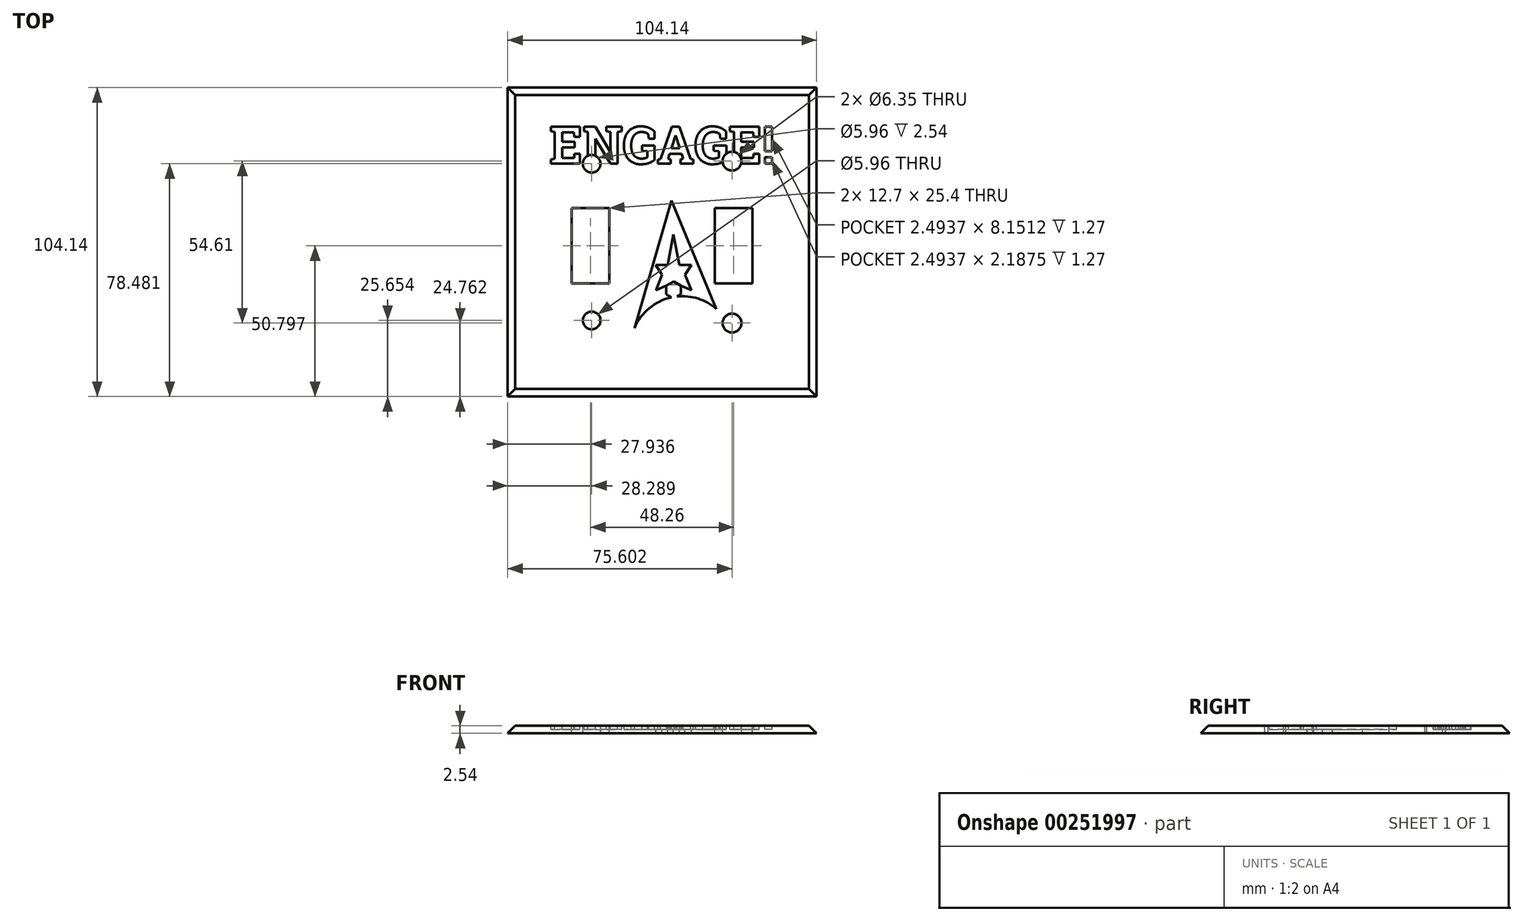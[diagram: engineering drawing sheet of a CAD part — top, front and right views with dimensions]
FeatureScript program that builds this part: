
annotation { "Feature Type Name" : "Feature", "Feature Type Description" : "" }
export const myFeature = defineFeature(function(context is Context, id is Id, definition is map)
    precondition{}
    {
        {
            var Q0;
            Q0=qCreatedBy(makeId("Top.planeOp"),FACE);
            var sketch = newSketch(context, id + "F0", { "sketchPlane" : qUnion([Q0])});
            skLineSegment(sketch, "E0.bottom", {"start": v(-65.17, 86.13) * mm, "end": v(49.13, 86.13) * mm});
            skLineSegment(sketch, "E0.top", {"start": v(-65.17, -28.17) * mm, "end": v(49.13, -28.17) * mm});
            skLineSegment(sketch, "E0.left", {"start": v(-65.17, 86.13) * mm, "end": v(-65.17, -28.17) * mm});
            skLineSegment(sketch, "E0.right", {"start": v(49.13, 86.13) * mm, "end": v(49.13, -28.17) * mm});
            skSolve(sketch);
        }
        {
            var Q0;
            Q0=makeQuery(id+"F0.imprint","IMPRINT",FACE,{"disambiguationData":[TD([[makeQuery(id+"F0.imprint","IMPRINT",EDGE,{"derivedFrom":sQuery(id+"F0.wireOp",EDGE,"E0.bottom")}),-1.0]])]});
            extrude(context, id + "F1", {"entities" : qUnion([Q0]), "depth" : 2.54 * mm});
        }
        {
            var Q0;
            Q0=makeQuery(id+"F1.opExtrude","CAP_EDGE",EDGE,{"disambiguationData":[OSD([sQuery(id+"F0.wireOp",EDGE,"E0.top")])],"isStart":false});
            var Q1;
            Q1=makeQuery(id+"F1.opExtrude","CAP_EDGE",EDGE,{"disambiguationData":[OSD([sQuery(id+"F0.wireOp",EDGE,"E0.left")])],"isStart":false});
            var Q2;
            Q2=makeQuery(id+"F1.opExtrude","CAP_EDGE",EDGE,{"disambiguationData":[OSD([sQuery(id+"F0.wireOp",EDGE,"E0.right")])],"isStart":false});
            var Q3;
            Q3=makeQuery(id+"F1.opExtrude","CAP_EDGE",EDGE,{"disambiguationData":[OSD([sQuery(id+"F0.wireOp",EDGE,"E0.bottom")])],"isStart":false});
            chamfer(context, id + "F2", {"entities" : qUnion([Q0, Q1, Q2, Q3]), "width" : 7.62 * mm, "tangentPropagation" : true});
        }
        {
            var Q0;
            Q0=makeQuery(id+"F1.opExtrude","CAP_FACE",FACE,{"disambiguationData":[OSD([sQuery(id+"F0.wireOp",EDGE,"E0.bottom"),sQuery(id+"F0.wireOp",EDGE,"E0.top"),sQuery(id+"F0.wireOp",EDGE,"E0.left"),sQuery(id+"F0.wireOp",EDGE,"E0.right")])],"isStart":false});
            var sketch = newSketch(context, id + "F3", { "sketchPlane" : qUnion([Q0])});
            skLineSegment(sketch, "E1.bottom", {"start": v(-25.8, 15) * mm, "end": v(-38.5, 15) * mm});
            skLineSegment(sketch, "E1.top", {"start": v(-25.8, 40.4) * mm, "end": v(-38.5, 40.4) * mm});
            skLineSegment(sketch, "E1.left", {"start": v(-25.8, 15) * mm, "end": v(-25.8, 40.4) * mm});
            skLineSegment(sketch, "E1.right", {"start": v(-38.5, 15) * mm, "end": v(-38.5, 40.4) * mm});
            skLineSegment(sketch, "E2.bottom", {"start": v(9.76, 40.4) * mm, "end": v(22.46, 40.4) * mm});
            skLineSegment(sketch, "E2.top", {"start": v(9.76, 15) * mm, "end": v(22.46, 15) * mm});
            skLineSegment(sketch, "E2.left", {"start": v(9.76, 40.4) * mm, "end": v(9.76, 15) * mm});
            skLineSegment(sketch, "E2.right", {"start": v(22.46, 40.4) * mm, "end": v(22.46, 15) * mm});
            skSolve(sketch);
        }
        {
            var Q0;
            Q0 = qSketchRegion(id + "F3", true);
            extrude(context, id + "F4", {"entities" : qUnion([Q0]), "operationType" : NewBodyOperationType.REMOVE, "oppositeDirection" : true, "depth" : 25.4 * mm});
        }
        {
            var Q0;
            Q0=makeQuery(id+"F1.opExtrude","CAP_FACE",FACE,{"disambiguationData":[OSD([sQuery(id+"F0.wireOp",EDGE,"E0.bottom"),sQuery(id+"F0.wireOp",EDGE,"E0.top"),sQuery(id+"F0.wireOp",EDGE,"E0.left"),sQuery(id+"F0.wireOp",EDGE,"E0.right")])],"isStart":false});
            var sketch = newSketch(context, id + "F5", { "sketchPlane" : qUnion([Q0])});
            skText(sketch, "E3", { "text": "ENGAGE!", "fontName": "RobotoSlab-Bold.ttf"});
            const initialGuessF5  = {"E3": [-0.04604, 0.0554, 1, 0, 0.0126]};
            skSetInitialGuess(sketch, initialGuessF5);
            skSolve(sketch);
        }
        {
            var Q0;
            Q0 = qSketchRegion(id + "F5", true);
            extrude(context, id + "F6", {"entities" : qUnion([Q0]), "operationType" : NewBodyOperationType.REMOVE, "oppositeDirection" : true, "depth" : 1.27 * mm});
        }
        {
            var Q0;
            {var subQ0=sQuery(id+"F0.wireOp",EDGE,"E0.right");var subQ1=sQuery(id+"F0.wireOp",EDGE,"E0.left");var subQ2=sQuery(id+"F0.wireOp",EDGE,"E0.top");var subQ3=sQuery(id+"F0.wireOp",EDGE,"E0.bottom");Q0=makeQuery(id+"F6.boolean.opBoolean","SPLIT",FACE,{"disambiguationData":[TD([makeQuery(id+"F2.opChamfer","BLEND_FACE",FACE,{"disambiguationData":[OSD([subQ3])]})])],"derivedFrom":makeQuery(id+"F1.opExtrude","CAP_FACE",FACE,{"disambiguationData":[OSD([subQ3,subQ2,subQ1,subQ0])],"isStart":false})});}
            var sketch = newSketch(context, id + "F7", { "sketchPlane" : qUnion([Q0])});
            skArc(sketch, "E4", {"start": v(10.26, 6.47) * mm, "mid": v(-5.2, 10.28) * mm, "end": v(-17.36, 0) * mm});
            skLineSegment(sketch, "E5", {"start": v(-17.36, 0) * mm, "end": v(-4.93, 42.96) * mm});
            skLineSegment(sketch, "E6", {"start": v(-4.93, 42.96) * mm, "end": v(10.26, 6.47) * mm});
            skPoint(sketch, "E7.startSnap0", {"position": v(-11.15, 21.48) * mm});
            skCircle(sketch, "E8.cCircle", {"center": v(-4.21, 17.91) * mm, "radius": 3.35 * mm, "construction": true});
            skLineSegment(sketch, "E8.0", {"start": v(-2.27, 14.56) * mm, "end": v(-6.15, 14.56) * mm});
            skLineSegment(sketch, "E8.1", {"start": v(-6.15, 14.56) * mm, "end": v(-8.08, 17.91) * mm});
            skLineSegment(sketch, "E8.2", {"start": v(-8.08, 17.91) * mm, "end": v(-6.15, 21.27) * mm});
            skLineSegment(sketch, "E8.3", {"start": v(-6.15, 21.27) * mm, "end": v(-2.27, 21.27) * mm});
            skLineSegment(sketch, "E8.4", {"start": v(-2.27, 21.27) * mm, "end": v(-0.34, 17.91) * mm});
            skLineSegment(sketch, "E8.5", {"start": v(-0.34, 17.91) * mm, "end": v(-2.27, 14.56) * mm});
            skPoint(sketch, "E8.0.midPoint", {"position": v(-4.21, 14.56) * mm});
            skLineSegment(sketch, "E9", {"start": v(-8.08, 17.91) * mm, "end": v(-10.06, 12.78) * mm});
            skLineSegment(sketch, "E10", {"start": v(-10.06, 12.78) * mm, "end": v(-6.15, 14.56) * mm});
            skLineSegment(sketch, "E11", {"start": v(-2.27, 14.56) * mm, "end": v(1.8, 12.72) * mm});
            skLineSegment(sketch, "E12", {"start": v(1.8, 12.72) * mm, "end": v(-0.34, 17.91) * mm});
            skLineSegment(sketch, "E13", {"start": v(-8.08, 17.91) * mm, "end": v(-10.23, 21.22) * mm});
            skLineSegment(sketch, "E14", {"start": v(-10.23, 21.22) * mm, "end": v(-6.15, 21.27) * mm});
            skLineSegment(sketch, "E15", {"start": v(-2.27, 21.27) * mm, "end": v(1.8, 21.27) * mm});
            skLineSegment(sketch, "E16", {"start": v(1.8, 21.27) * mm, "end": v(-0.34, 17.91) * mm});
            skLineSegment(sketch, "E17", {"start": v(-6.15, 21.27) * mm, "end": v(-4.33, 31.55) * mm});
            skLineSegment(sketch, "E18", {"start": v(-4.33, 31.55) * mm, "end": v(-2.27, 21.27) * mm});
            skSolve(sketch);
        }
        {
            var Q0;
            Q0=makeQuery(id+"F7.imprint","IMPRINT",FACE,{"disambiguationData":[TD([[makeQuery(id+"F7.imprint","IMPRINT",EDGE,{"derivedFrom":sQuery(id+"F7.wireOp",EDGE,"E4")}),-1.0]])]});
            extrude(context, id + "F8", {"entities" : qUnion([Q0]), "operationType" : NewBodyOperationType.REMOVE, "oppositeDirection" : true, "depth" : 1.27 * mm});
        }
        {
            var Q0;
            {var subQ0=sQuery(id+"F0.wireOp",EDGE,"E0.right");var subQ1=sQuery(id+"F0.wireOp",EDGE,"E0.left");var subQ2=sQuery(id+"F0.wireOp",EDGE,"E0.top");var subQ3=sQuery(id+"F0.wireOp",EDGE,"E0.bottom");Q0=makeQuery(id+"F8.boolean.opBoolean","SPLIT",FACE,{"disambiguationData":[TD([makeQuery(id+"F8.opExtrude","SWEPT_FACE",FACE,{"disambiguationData":[OSD([sQuery(id+"F7.wireOp",EDGE,"E8.0")])]})])],"derivedFrom":makeQuery(id+"F6.boolean.opBoolean","SPLIT",FACE,{"disambiguationData":[TD([makeQuery(id+"F2.opChamfer","BLEND_FACE",FACE,{"disambiguationData":[OSD([subQ3])]})])],"derivedFrom":makeQuery(id+"F1.opExtrude","CAP_FACE",FACE,{"disambiguationData":[OSD([subQ3,subQ2,subQ1,subQ0])],"isStart":false})})});}
            extrude(context, id + "F9", {"entities" : qUnion([Q0]), "operationType" : NewBodyOperationType.REMOVE, "oppositeDirection" : true, "depth" : 25.4 * mm});
        }
        {
            var Q0;
            Q0=makeQuery(id+"F8.boolean.opBoolean","COPY",FACE,{"derivedFrom":makeQuery(id+"F8.opExtrude","CAP_FACE",FACE,{"disambiguationData":[OSD([sQuery(id+"F7.wireOp",EDGE,"E4"),sQuery(id+"F7.wireOp",EDGE,"E5"),sQuery(id+"F7.wireOp",EDGE,"E6"),sQuery(id+"F7.wireOp",EDGE,"E8.0"),sQuery(id+"F7.wireOp",EDGE,"E9"),sQuery(id+"F7.wireOp",EDGE,"E10"),sQuery(id+"F7.wireOp",EDGE,"E11"),sQuery(id+"F7.wireOp",EDGE,"E12"),sQuery(id+"F7.wireOp",EDGE,"E13"),sQuery(id+"F7.wireOp",EDGE,"E14"),sQuery(id+"F7.wireOp",EDGE,"E15"),sQuery(id+"F7.wireOp",EDGE,"E16"),sQuery(id+"F7.wireOp",EDGE,"E17"),sQuery(id+"F7.wireOp",EDGE,"E18")])],"isStart":false})});
            var sketch = newSketch(context, id + "F10", { "sketchPlane" : qUnion([Q0])});
            skCircle(sketch, "E19.cCircle", {"center": v(-4.17, 12.85) * mm, "radius": 2.5 * mm, "construction": true});
            skLineSegment(sketch, "E19.0", {"start": v(-1.68, 14.29) * mm, "end": v(-1.68, 11.41) * mm});
            skLineSegment(sketch, "E19.1", {"start": v(-1.68, 11.41) * mm, "end": v(-4.17, 9.97) * mm});
            skLineSegment(sketch, "E19.2", {"start": v(-4.17, 9.97) * mm, "end": v(-6.66, 11.41) * mm});
            skLineSegment(sketch, "E19.3", {"start": v(-6.66, 11.41) * mm, "end": v(-6.66, 14.29) * mm});
            skLineSegment(sketch, "E19.4", {"start": v(-6.66, 14.29) * mm, "end": v(-4.17, 15.73) * mm});
            skLineSegment(sketch, "E19.5", {"start": v(-4.17, 15.73) * mm, "end": v(-1.68, 14.29) * mm});
            skPoint(sketch, "E19.0.midPoint", {"position": v(-1.68, 12.85) * mm});
            skSolve(sketch);
        }
        {
            var Q0;
            Q0 = qSketchRegion(id + "F10", true);
            extrude(context, id + "F11", {"entities" : qUnion([Q0]), "operationType" : NewBodyOperationType.ADD, "depth" : 1.27 * mm});
        }
        {
            var Q0;
            {var subQ6=sQuery(id+"F0.wireOp",EDGE,"E0.top");var subQ29=sQuery(id+"F0.wireOp",EDGE,"E0.left");var subQ73=sQuery(id+"F0.wireOp",EDGE,"E0.right");var subQ95=sQuery(id+"F0.wireOp",EDGE,"E0.bottom");var subQ96=makeQuery(id+"F2.opChamfer","BLEND_FACE",FACE,{"disambiguationData":[OSD([subQ95])]});Q0=makeQuery(id+"F11.boolean.opBoolean","MERGE",FACE,{"derivedFrom":[makeQuery(id+"F8.boolean.opBoolean","SPLIT",FACE,{"disambiguationData":[TD([subQ96])],"derivedFrom":makeQuery(id+"F6.boolean.opBoolean","SPLIT",FACE,{"disambiguationData":[TD([subQ96])],"derivedFrom":makeQuery(id+"F1.opExtrude","CAP_FACE",FACE,{"disambiguationData":[OSD([subQ95,subQ6,subQ29,subQ73])],"isStart":false})})}),makeQuery(id+"F11.opExtrude","CAP_FACE",FACE,{"disambiguationData":[OSD([sQuery(id+"F10.wireOp",EDGE,"E19.0"),sQuery(id+"F10.wireOp",EDGE,"E19.1"),sQuery(id+"F10.wireOp",EDGE,"E19.2"),sQuery(id+"F10.wireOp",EDGE,"E19.3"),sQuery(id+"F10.wireOp",EDGE,"E19.4"),sQuery(id+"F10.wireOp",EDGE,"E19.5")])],"isStart":false})]});}
            var sketch = newSketch(context, id + "F12", { "sketchPlane" : qUnion([Q0])});
            skCircle(sketch, "E20", {"center": v(15.51, 56.28) * mm, "radius": 3.18 * mm});
            skCircle(sketch, "E21", {"center": v(-31.8, 55.4) * mm, "radius": 2.98 * mm});
            skLineSegment(sketch, "E22", {"start": v(-57.55, 28.98) * mm, "end": v(41.5, 28.98) * mm, "construction": true});
            skCircle(sketch, "E23.MirrorC", {"center": v(-31.8, 2.56) * mm, "radius": 2.98 * mm});
            skCircle(sketch, "E24.MirrorC", {"center": v(15.51, 1.67) * mm, "radius": 3.18 * mm});
            skSolve(sketch);
        }
        {
            var Q0;
            Q0 = qSketchRegion(id + "F12", true);
            extrude(context, id + "F13", {"entities" : qUnion([Q0]), "operationType" : NewBodyOperationType.REMOVE, "oppositeDirection" : true, "depth" : 25.4 * mm});
        }
    });
